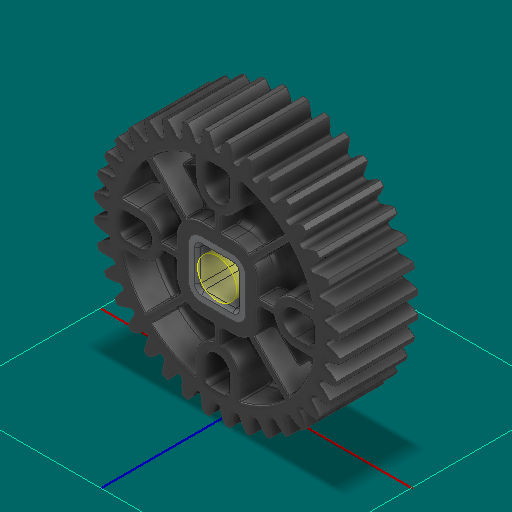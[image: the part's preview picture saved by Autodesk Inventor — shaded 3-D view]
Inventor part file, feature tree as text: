
AUTODESK INVENTOR PART (.ipt)
format: ipt  version: 2025 (Build 290162000, 162)  size: 3,322,880 bytes
history: native  units: in
note: dims shown in document units (in); Inventor stores cm internally (conversion verified against a paired STEP export)
features: other x6, sketch x1
ambient origin geometry x8: Origin, YZ Plane, XZ Plane, XY Plane, X Axis, Y Axis, Z Axis, Center Point
bodies: Solid1 (feature_tree), Solid2 (feature_tree)
feature tree (7):
  other  "HS 36T Gear, No Insert.ipt"
  other  "Solid1::HS 36T Gear, No Insert.ipt"
  other  "Solid2::HS 36T Gear, No Insert.ipt"
  other  "TaggingFeature1"
  sketch  "Sketch1"  dims[d0=0.3937in]
  other  "Srf1"
  other  "Srf1::Derived"
